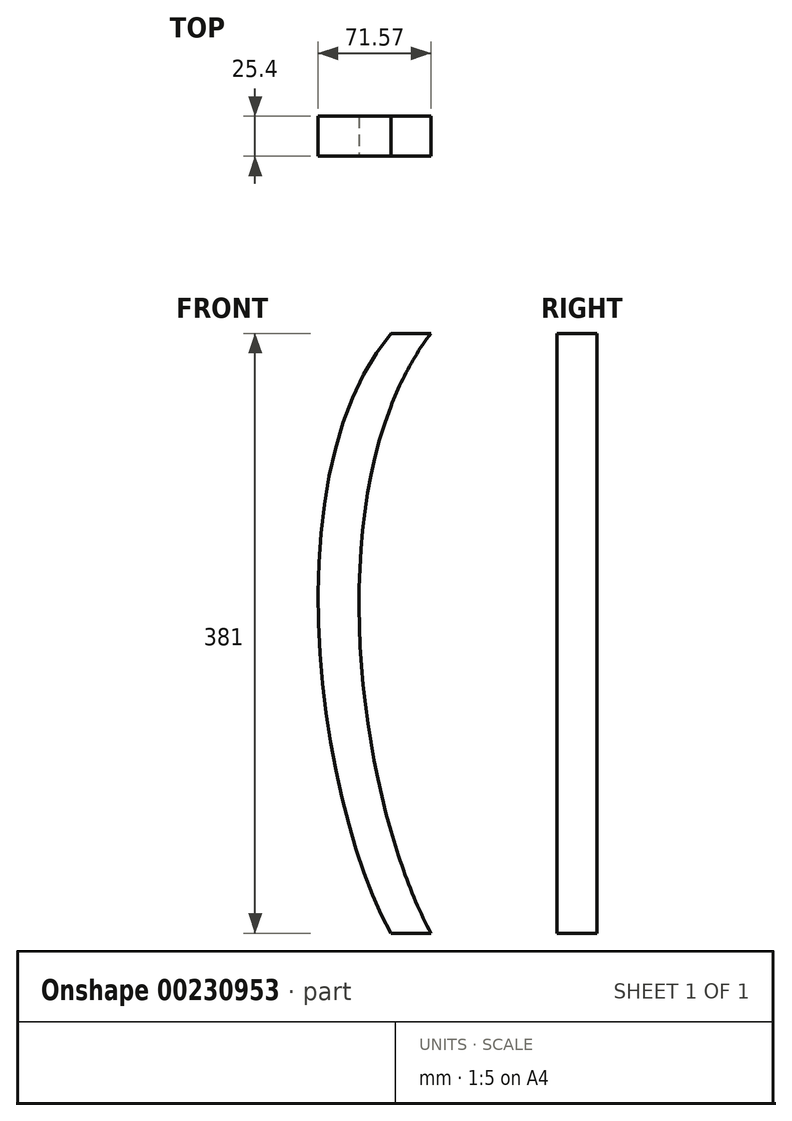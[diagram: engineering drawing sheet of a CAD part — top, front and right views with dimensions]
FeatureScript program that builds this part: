
annotation { "Feature Type Name" : "Feature", "Feature Type Description" : "" }
export const myFeature = defineFeature(function(context is Context, id is Id, definition is map)
    precondition{}
    {
        {
            var Q0;
            Q0=qCreatedBy(makeId("Front.planeOp"),FACE);
            var sketch = newSketch(context, id + "F0", { "sketchPlane" : qUnion([Q0])});
            skLineSegment(sketch, "E0.bottom", {"start": v(-177.8, 381) * mm, "end": v(-152.4, 381) * mm});
            skLineSegment(sketch, "E0.top", {"start": v(-177.8, 0) * mm, "end": v(-152.4, 0) * mm});
            skLineSegment(sketch, "E0.left", {"start": v(-177.8, 381) * mm, "end": v(-177.8, 0) * mm});
            skLineSegment(sketch, "E0.right", {"start": v(-152.4, 381) * mm, "end": v(-152.4, 0) * mm});
            skFitSpline(sketch, "E1", {"points": [v(-177.8, 381) * mm, v(-177.8, 0) * mm], "startDerivative": vector(-226.46, -272.88) * mm, "endDerivative": vector(137.67, -248.32) * mm});
            skFitSpline(sketch, "E2", {"points": [v(-152.4, 381) * mm, v(-152.4, 0) * mm], "startDerivative": vector(-218.65, -285.72) * mm, "endDerivative": vector(142.59, -265.9) * mm});
            skSolve(sketch);
        }
        {
            var Q0;
            {var subQ0=sQuery(id+"F0.wireOp",EDGE,"E0.bottom");Q0=makeQuery(id+"F0.imprint","IMPRINT",FACE,{"disambiguationData":[TD([[makeQuery(id+"F0.imprint","IMPRINT",EDGE,{"derivedFrom":subQ0}),-1.0]])]});}
            var Q1;
            {var subQ0=sQuery(id+"F0.wireOp",EDGE,"E0.top");Q1=makeQuery(id+"F0.imprint","IMPRINT",FACE,{"disambiguationData":[TD([[makeQuery(id+"F0.imprint","IMPRINT",EDGE,{"derivedFrom":subQ0}),1.0]])]});}
            var Q2;
            {var subQ0=sQuery(id+"F0.wireOp",EDGE,"E1");Q2=makeQuery(id+"F0.imprint","IMPRINT",FACE,{"disambiguationData":[TD([[makeQuery(id+"F0.imprint","IMPRINT",EDGE,{"derivedFrom":subQ0}),1.0]])]});}
            extrude(context, id + "F1", {"entities" : qUnion([Q0, Q1, Q2]), "endBound" : BoundingType.SYMMETRIC, "depth" : 25.4 * mm});
        }
    });
